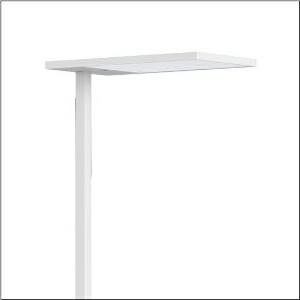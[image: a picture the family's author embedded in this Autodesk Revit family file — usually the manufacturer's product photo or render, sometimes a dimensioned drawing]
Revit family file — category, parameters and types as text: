
# Revit family: silica_r__21_floor_r_51mx53sg4ew_c996
name_source: partatom
category: Lighting Fixtures
units: mm (PartAtom-declared; Revit-internal decimal feet)

## family parameters
Cut with Voids When Loaded = No
Host = Face
Light Source = No
Part Type = Normal
Room Calculation Point = No
Round Connector Dimension = Use Diameter
Shared = No

## types (1)
- Silica® 21 Floor R (1 x LED, 15000 lm, 106.4 W, 4000K)
    Apparent Load = 106 VA
    CIE Flux Codes = 54 86 97 13 100
    Color Rendering = 80
    Color Temperature = 4000K
    Default Elevation = 1800 mm
    Description = Silica® 21 Floor R, floorstanding luminaire, of PMMA, primary optical cover: prismatic diffuser, of PMMA, CAT 2 (L<= 3000cd/m²), light emission: indirect/direct distribution, primary light characteristic: symmetric, primary optical cover: cover panel, of PMMA, installation type: not mounted, LED, rated luminous flux: 15.000lm, luminous efficacy: 141lm/W, light colour: 840, colour temperature: 4000K, control gear: DALI 2, daylight-dependent control, mains connection: 230V, AC, 50/60Hz, connection cable included, cable length: 2,5m, rated input power: 106.4W, luminaire head, of aluminium, powder-coated, traffic white (RAL 9016), length: 671mm, width: 371mm, height: 2010mm, supporting column, angular, of aluminium, powder-coated, traffic white (RAL 9016), baseplate, of steel, powder-coated, traffic white (RAL 9016), sensor module PR3-S, local control - self-sufficient standalone sensors, equipment: master, direct and indirect component separately switchable, protection rating (complete): IP20, insulation class (complete): insulation class I (protective earthing), certification: CE, standard: EN 50419, packaging unit: 1 piece
    Height = 18 mm
    Lamp = 1 x LED
    Lamp Light Flux = 15000 lm
    Lamp Power = 106.4 W
    Lamp count = 1
    Length = 650 mm
    Luminous efficacy = 141 lm/W
    Manufacturer = Siteco
    ModVariant = No
    Model = 51MX53SG4EW
    Mounting Place = Floor
    Mounting Type = Freestanding
    Number of Poles = 1
    OnlyDefault = Yes
    Power Factor = 1
    Product Name = Silica® 21 Floor R
    Product group = floorstanding luminaire
    ProductGroupID = 1302
    Protection Class = Protection class I
    Protection Degree = IP 20
    RLX_Detail_Level = 1
    RLX_Emergency_Light_Flux = 0 lm
    RLX_Emergency_Type = 0
    RLX_Emergency_Type_DB = No
    RlxData = <blob elided: 18949 chars, md5=016ac823>
    Socket = socket
    Standby Power = 0 W
    System Light Flux = 15000 lm
    System Power = 106 W
    Type Comments = Product without accessories
    Type Image = l_1003935.jpg
    URL = http://relux.com
    VarID = ---
    Voltage = 0 V
    Weight = 0.00 kg
    Width = 350 mm

## geometry (parser evidence)
native form markers: Blend x4, Sweep x14
no freeform markers — native parametric forms only
